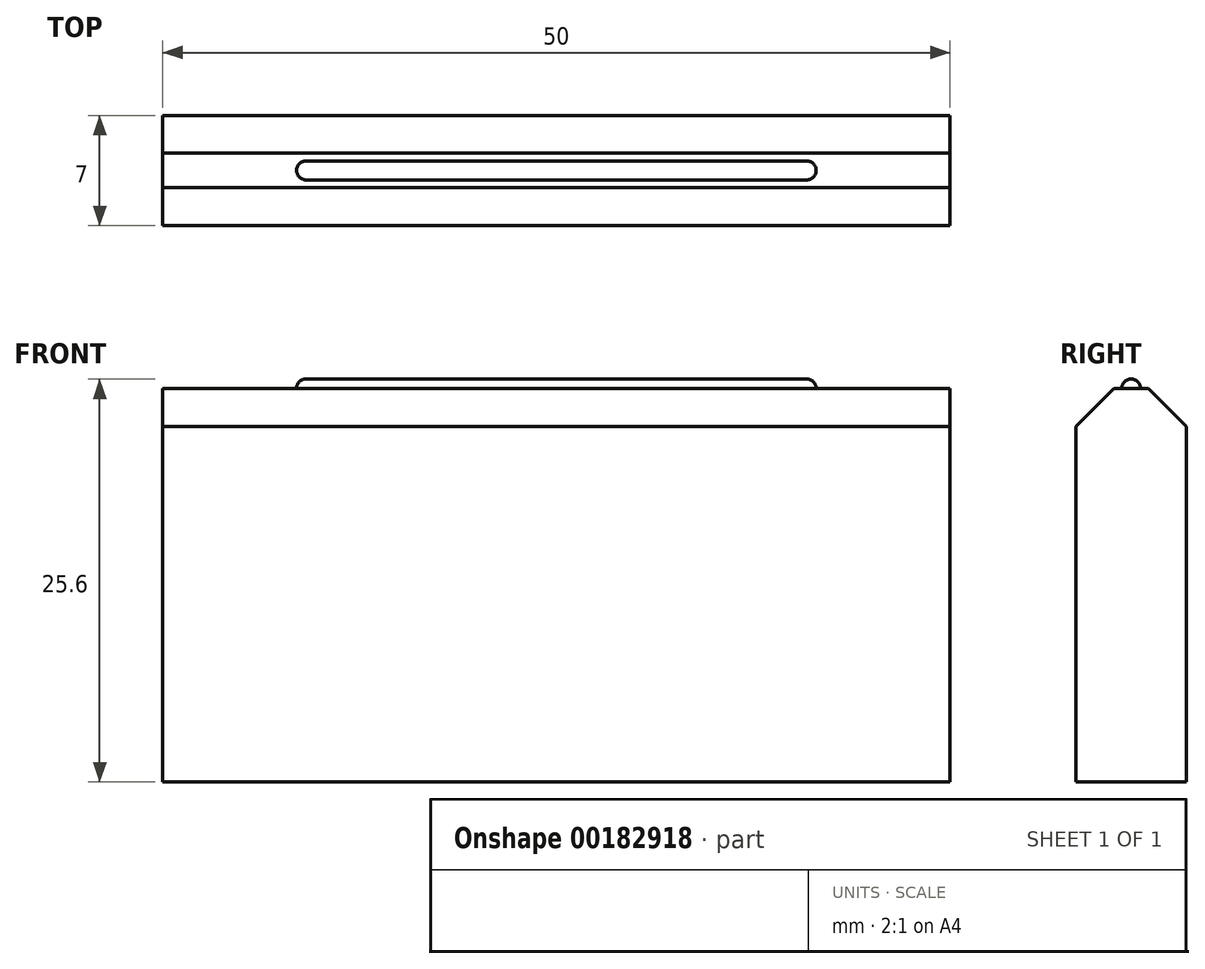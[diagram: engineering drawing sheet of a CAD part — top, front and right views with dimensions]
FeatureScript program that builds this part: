
annotation { "Feature Type Name" : "Feature", "Feature Type Description" : "" }
export const myFeature = defineFeature(function(context is Context, id is Id, definition is map)
    precondition{}
    {
        {
            var Q0;
            Q0=qCreatedBy(makeId("Top.planeOp"),FACE);
            var sketch = newSketch(context, id + "F0", { "sketchPlane" : qUnion([Q0])});
            skLineSegment(sketch, "E0.bottom", {"start": v(25, -3.5) * mm, "end": v(-25, -3.5) * mm});
            skLineSegment(sketch, "E0.top", {"start": v(25, 3.5) * mm, "end": v(-25, 3.5) * mm});
            skLineSegment(sketch, "E0.left", {"start": v(25, -3.5) * mm, "end": v(25, 3.5) * mm});
            skLineSegment(sketch, "E0.right", {"start": v(-25, -3.5) * mm, "end": v(-25, 3.5) * mm});
            skPoint(sketch, "E0.middle", {"position": v(0, 0) * mm});
            skSolve(sketch);
        }
        {
            var Q0;
            Q0 = qSketchRegion(id + "F0", true);
            extrude(context, id + "F1", {"entities" : qUnion([Q0]), "depth" : 25 * mm});
        }
        {
            var Q0;
            Q0=makeQuery(id+"F1.opExtrude","CAP_EDGE",EDGE,{"disambiguationData":[OSD([sQuery(id+"F0.wireOp",EDGE,"E0.bottom")])],"isStart":false});
            var Q1;
            Q1=makeQuery(id+"F1.opExtrude","CAP_EDGE",EDGE,{"disambiguationData":[OSD([sQuery(id+"F0.wireOp",EDGE,"E0.top")])],"isStart":false});
            chamfer(context, id + "F2", {"entities" : qUnion([Q0, Q1]), "width" : 2.4 * mm, "tangentPropagation" : true});
        }
        {
            var Q0;
            Q0=qCreatedBy(makeId("Right.planeOp"),FACE);
            var sketch = newSketch(context, id + "F3", { "sketchPlane" : qUnion([Q0])});
            skCircle(sketch, "E1", {"center": v(0, 25) * mm, "radius": 0.6 * mm});
            skSolve(sketch);
        }
        {
            var Q0;
            Q0=makeQuery(id+"F3.imprint","IMPRINT",FACE,{"disambiguationData":[TD([[makeQuery(id+"F3.imprint","IMPRINT",EDGE,{"derivedFrom":sQuery(id+"F3.wireOp",EDGE,"E1")}),1.0]])]});
            extrude(context, id + "F4", {"entities" : qUnion([Q0]), "operationType" : NewBodyOperationType.ADD, "endBound" : BoundingType.SYMMETRIC, "depth" : 33 * mm});
        }
        {
            var Q0;
            Q0=makeQuery(id+"F4.opExtrude","CAP_EDGE",EDGE,{"disambiguationData":[OSD([sQuery(id+"F3.wireOp",EDGE,"E1")])],"isStart":false});
            var Q1;
            Q1=makeQuery(id+"F4.opExtrude","CAP_EDGE",EDGE,{"disambiguationData":[OSD([sQuery(id+"F3.wireOp",EDGE,"E1")])],"isStart":true});
            fillet(context, id + "F5", {"entities" : qUnion([Q0, Q1]), "radius" : 0.6 * mm, "tangentPropagation" : true, "allowEdgeOverflow" : false});
        }
    });
